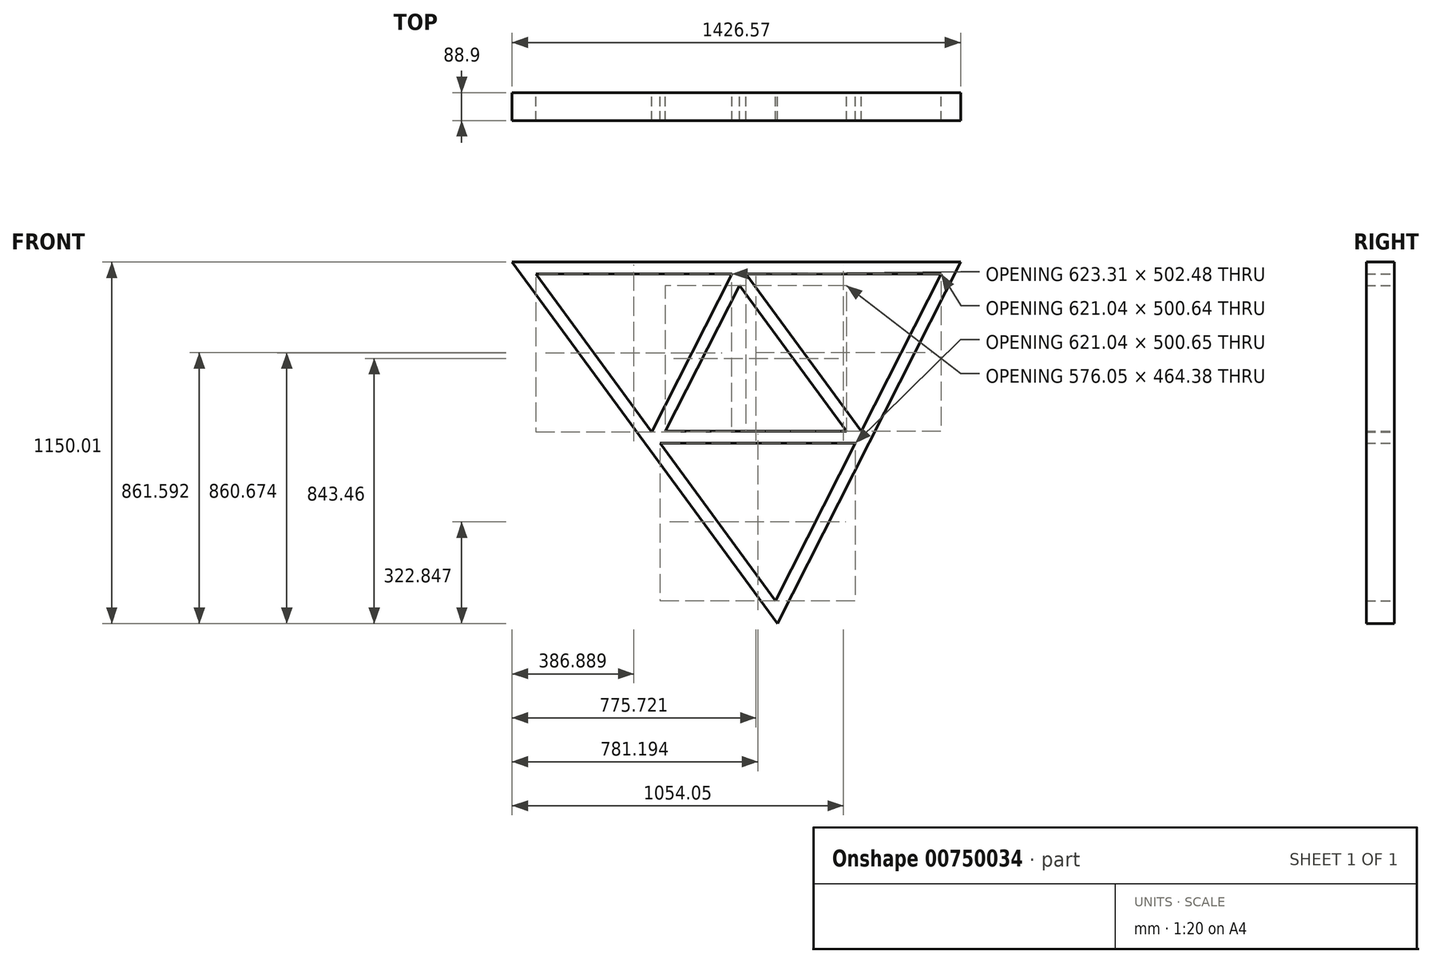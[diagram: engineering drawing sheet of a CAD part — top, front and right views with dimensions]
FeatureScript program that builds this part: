
annotation { "Feature Type Name" : "Feature", "Feature Type Description" : "" }
export const myFeature = defineFeature(function(context is Context, id is Id, definition is map)
    precondition{}
    {
        {
            var Q0;
            Q0=qCreatedBy(makeId("Front.planeOp"),FACE);
            var sketch = newSketch(context, id + "F0", { "sketchPlane" : qUnion([Q0])});
            skLineSegment(sketch, "E0", {"start": v(-765.03, 381.4) * mm, "end": v(661.54, 381.4) * mm});
            skLineSegment(sketch, "E1", {"start": v(661.54, 381.4) * mm, "end": v(79.1, -768.62) * mm});
            skLineSegment(sketch, "E2", {"start": v(79.1, -768.62) * mm, "end": v(-765.03, 381.4) * mm});
            skLineSegment(sketch, "E3", {"start": v(73.12, -696.1) * mm, "end": v(599.54, 343.3) * mm});
            skLineSegment(sketch, "E4", {"start": v(599.54, 343.3) * mm, "end": v(-689.8, 343.3) * mm});
            skLineSegment(sketch, "E5", {"start": v(-689.8, 343.3) * mm, "end": v(73.12, -696.1) * mm});
            skLineSegment(sketch, "E6", {"start": v(-21.5, 343.3) * mm, "end": v(345.98, -157.35) * mm});
            skLineSegment(sketch, "E7", {"start": v(345.98, -157.35) * mm, "end": v(326.68, -195.45) * mm});
            skLineSegment(sketch, "E8", {"start": v(326.68, -195.45) * mm, "end": v(-294.35, -195.45) * mm});
            skLineSegment(sketch, "E9", {"start": v(-294.35, -195.45) * mm, "end": v(-320.97, -159.19) * mm});
            skLineSegment(sketch, "E10", {"start": v(-320.97, -159.19) * mm, "end": v(-66.48, 343.3) * mm});
            skLineSegment(sketch, "E11", {"start": v(298.72, -157.35) * mm, "end": v(-68.76, 343.3) * mm});
            skLineSegment(sketch, "E12", {"start": v(-42.14, 307.03) * mm, "end": v(-295.7, -193.61) * mm});
            skLineSegment(sketch, "E13", {"start": v(-277.33, -157.35) * mm, "end": v(345.98, -157.35) * mm});
            skSolve(sketch);
        }
        {
            var Q0;
            Q0=makeQuery(id+"F0.imprint","IMPRINT",FACE,{"disambiguationData":[TD([[makeQuery(id+"F0.imprint","IMPRINT",EDGE,{"derivedFrom":sQuery(id+"F0.wireOp",EDGE,"E0")}),-1.0]])]});
            var Q1;
            {var subQ3=sQuery(id+"F0.wireOp",EDGE,"E10");var subQ6=sQuery(id+"F0.wireOp",EDGE,"E5");var subQ7=makeQuery(id+"F0.imprint","INTERSECT",VERTEX,{"derivedFrom":[subQ6,subQ3]});Q1=makeQuery(id+"F0.imprint","IMPRINT",FACE,{"disambiguationData":[TD([[makeQuery(id+"F0.imprint","IMPRINT",EDGE,{"disambiguationData":[TD([[subQ7,-1.0]])],"derivedFrom":subQ6}),1.0]])]});}
            var Q2;
            {var subQ5=sQuery(id+"F0.wireOp",EDGE,"E6");Q2=makeQuery(id+"F0.imprint","IMPRINT",FACE,{"disambiguationData":[TD([[makeQuery(id+"F0.imprint","IMPRINT",EDGE,{"derivedFrom":subQ5}),-1.0]])]});}
            var Q3;
            {var subQ5=sQuery(id+"F0.wireOp",EDGE,"E8");Q3=makeQuery(id+"F0.imprint","IMPRINT",FACE,{"disambiguationData":[TD([[makeQuery(id+"F0.imprint","IMPRINT",EDGE,{"derivedFrom":subQ5}),-1.0]])]});}
            extrude(context, id + "F1", {"entities" : qUnion([Q0, Q1, Q2, Q3]), "endBound" : BoundingType.SYMMETRIC, "depth" : 88.9 * mm, "offsetDistance" : 25.4 * mm});
        }
    });
